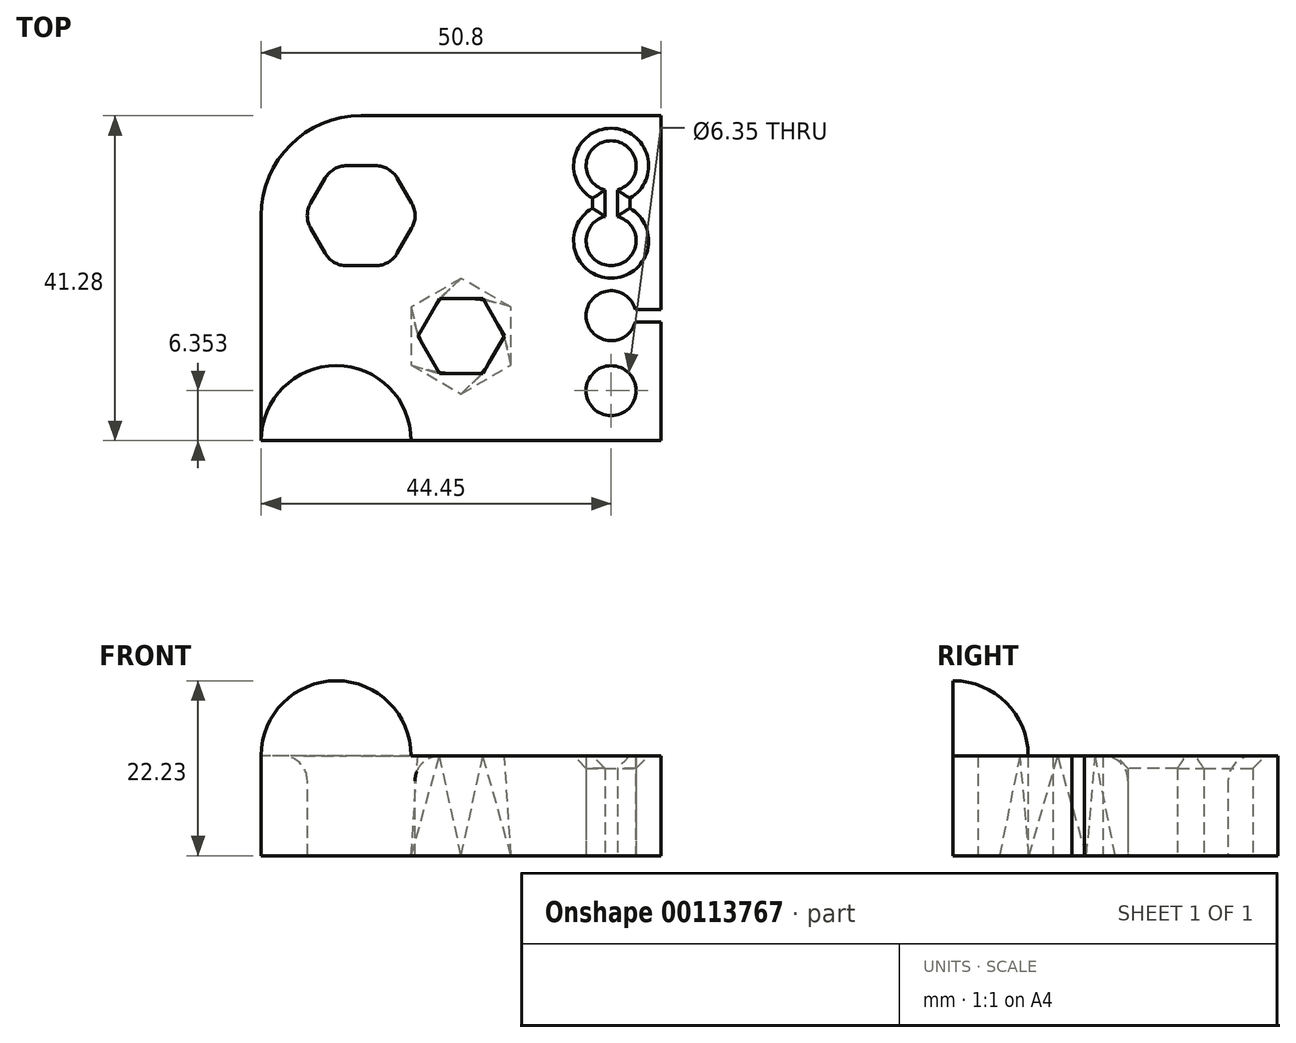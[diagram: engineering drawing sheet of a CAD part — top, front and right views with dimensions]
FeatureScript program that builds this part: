
annotation { "Feature Type Name" : "Feature", "Feature Type Description" : "" }
export const myFeature = defineFeature(function(context is Context, id is Id, definition is map)
    precondition{}
    {
        {
            var Q0;
            Q0=qCreatedBy(makeId("Top.planeOp"),FACE);
            var sketch = newSketch(context, id + "F0", { "sketchPlane" : qUnion([Q0])});
            skLineSegment(sketch, "E0.bottom", {"start": v(-12.7, 20.64) * mm, "end": v(25.4, 20.64) * mm});
            skLineSegment(sketch, "E0.top", {"start": v(-25.4, -20.64) * mm, "end": v(25.4, -20.64) * mm});
            skLineSegment(sketch, "E0.left", {"start": v(-25.4, 7.94) * mm, "end": v(-25.4, -20.64) * mm});
            skLineSegment(sketch, "E0.right", {"start": v(25.4, 20.64) * mm, "end": v(25.4, -20.64) * mm});
            skPoint(sketch, "E0.middle", {"position": v(0, 0) * mm});
            skCircle(sketch, "E1", {"center": v(19.05, -14.29) * mm, "radius": 3.18 * mm});
            skCircle(sketch, "E2.0.1.0", {"center": v(19.05, -4.76) * mm, "radius": 3.18 * mm});
            skCircle(sketch, "E2.0.2.0", {"center": v(19.05, 4.76) * mm, "radius": 3.18 * mm});
            skCircle(sketch, "E2.0.3.0", {"center": v(19.05, 14.29) * mm, "radius": 3.18 * mm});
            skLineSegment(sketch, "E2.direction1", {"start": v(19.05, -14.29) * mm, "end": v(36.43, -14.29) * mm, "construction": true});
            skLineSegment(sketch, "E2.direction2", {"start": v(19.05, -14.29) * mm, "end": v(19.05, -4.76) * mm, "construction": true});
            skLineSegment(sketch, "E3.bottom", {"start": v(18.26, -14.29) * mm, "end": v(19.84, -14.29) * mm});
            skLineSegment(sketch, "E3.top", {"start": v(18.26, 14.29) * mm, "end": v(19.84, 14.29) * mm});
            skLineSegment(sketch, "E3.left", {"start": v(18.26, -14.29) * mm, "end": v(18.26, 14.29) * mm});
            skLineSegment(sketch, "E3.right", {"start": v(19.84, -14.29) * mm, "end": v(19.84, 14.29) * mm});
            skLineSegment(sketch, "E4.bottom", {"start": v(19.05, -3.97) * mm, "end": v(25.4, -3.97) * mm});
            skLineSegment(sketch, "E4.top", {"start": v(19.05, -5.56) * mm, "end": v(25.4, -5.56) * mm});
            skLineSegment(sketch, "E4.left", {"start": v(19.05, -3.97) * mm, "end": v(19.05, -5.56) * mm});
            skLineSegment(sketch, "E4.right", {"start": v(25.4, -3.97) * mm, "end": v(25.4, -5.56) * mm});
            skPoint(sketch, "E5.visualSharp", {"position": v(-25.4, 20.64) * mm});
            skArc(sketch, "E5.filletArc", {"start": v(-12.7, 20.64) * mm, "mid": v(-21.68, 16.92) * mm, "end": v(-25.4, 7.94) * mm});
            skCircle(sketch, "E6", {"center": v(-12.7, 7.94) * mm, "radius": 6.35 * mm, "construction": true});
            skLineSegment(sketch, "E7.0", {"start": v(-9.03, 1.59) * mm, "end": v(-16.37, 1.59) * mm});
            skLineSegment(sketch, "E7.1", {"start": v(-16.37, 1.59) * mm, "end": v(-20.03, 7.94) * mm});
            skLineSegment(sketch, "E7.2", {"start": v(-20.03, 7.94) * mm, "end": v(-16.37, 14.29) * mm});
            skLineSegment(sketch, "E7.3", {"start": v(-16.37, 14.29) * mm, "end": v(-9.03, 14.29) * mm});
            skLineSegment(sketch, "E7.4", {"start": v(-9.03, 14.29) * mm, "end": v(-5.37, 7.94) * mm});
            skLineSegment(sketch, "E7.5", {"start": v(-5.37, 7.94) * mm, "end": v(-9.03, 1.59) * mm});
            skPoint(sketch, "E7.0.midPoint", {"position": v(-12.7, 1.59) * mm});
            skSolve(sketch);
        }
        {
            var Q0;
            {var subQ27=sQuery(id+"F0.wireOp",EDGE,"E0.bottom");Q0=makeQuery(id+"F0.imprint","IMPRINT",FACE,{"disambiguationData":[TD([[makeQuery(id+"F0.imprint","IMPRINT",EDGE,{"derivedFrom":subQ27}),-1.0]])]});}
            var Q1;
            {var subQ0=sQuery(id+"F0.wireOp",EDGE,"E3.left");var subQ1=sQuery(id+"F0.wireOp",EDGE,"E1");var subQ2=makeQuery(id+"F0.imprint","INTERSECT",VERTEX,{"derivedFrom":[subQ1,subQ0]});Q1=makeQuery(id+"F0.imprint","IMPRINT",FACE,{"disambiguationData":[TD([[makeQuery(id+"F0.imprint","IMPRINT",EDGE,{"disambiguationData":[TD([[subQ2,1.0]])],"derivedFrom":subQ1}),-1.0]])]});}
            var Q2;
            {var subQ0=sQuery(id+"F0.wireOp",EDGE,"E3.right");var subQ1=sQuery(id+"F0.wireOp",EDGE,"E2.0.1.0");var subQ2=makeQuery(id+"F0.imprint","INTERSECT",VERTEX,{"disambiguationData":[OD(0.0)],"derivedFrom":[subQ1,subQ0]});Q2=makeQuery(id+"F0.imprint","IMPRINT",FACE,{"disambiguationData":[TD([[makeQuery(id+"F0.imprint","IMPRINT",EDGE,{"disambiguationData":[TD([[subQ2,-1.0]])],"derivedFrom":subQ1}),-1.0]])]});}
            extrude(context, id + "F1", {"entities" : qUnion([Q0, Q1, Q2]), "depth" : 12.7 * mm});
        }
        {
            var Q0;
            Q0=makeQuery(id+"F1.opExtrude","CAP_EDGE",EDGE,{"disambiguationData":[OSD([sQuery(id+"F0.wireOp",EDGE,"E2.0.2.0")])],"isStart":false});
            var Q1;
            Q1=makeQuery(id+"F1.opExtrude","CAP_EDGE",EDGE,{"disambiguationData":[OSD([sQuery(id+"F0.wireOp",EDGE,"E2.0.3.0")])],"isStart":false});
            var Q2;
            Q2=makeQuery(id+"F1.opExtrude","CAP_EDGE",EDGE,{"disambiguationData":[OSD([sQuery(id+"F0.wireOp",EDGE,"E3.left")])],"isStart":false});
            var Q3;
            Q3=makeQuery(id+"F1.opExtrude","CAP_EDGE",EDGE,{"disambiguationData":[OSD([sQuery(id+"F0.wireOp",EDGE,"E3.right")])],"isStart":false});
            chamfer(context, id + "F2", {"entities" : qUnion([Q0, Q1, Q2, Q3]), "width" : 1.59 * mm, "tangentPropagation" : true});
        }
        {
            var Q0;
            Q0=makeQuery(id+"F1.opExtrude","CAP_EDGE",EDGE,{"disambiguationData":[OSD([sQuery(id+"F0.wireOp",EDGE,"E7.5")])],"isStart":false});
            var Q1;
            Q1=makeQuery(id+"F1.opExtrude","CAP_EDGE",EDGE,{"disambiguationData":[OSD([sQuery(id+"F0.wireOp",EDGE,"E7.4")])],"isStart":false});
            var Q2;
            Q2=makeQuery(id+"F1.opExtrude","CAP_EDGE",EDGE,{"disambiguationData":[OSD([sQuery(id+"F0.wireOp",EDGE,"E7.3")])],"isStart":false});
            var Q3;
            Q3=makeQuery(id+"F1.opExtrude","CAP_EDGE",EDGE,{"disambiguationData":[OSD([sQuery(id+"F0.wireOp",EDGE,"E7.2")])],"isStart":false});
            var Q4;
            Q4=makeQuery(id+"F1.opExtrude","CAP_EDGE",EDGE,{"disambiguationData":[OSD([sQuery(id+"F0.wireOp",EDGE,"E7.1")])],"isStart":false});
            var Q5;
            Q5=makeQuery(id+"F1.opExtrude","CAP_EDGE",EDGE,{"disambiguationData":[OSD([sQuery(id+"F0.wireOp",EDGE,"E7.0")])],"isStart":false});
            var Q6;
            Q6=makeQuery(id+"F1.opExtrude","SWEPT_EDGE",EDGE,{"disambiguationData":[OSD([sQuery(id+"F0.wireOp",EDGE,"E7.2"),sQuery(id+"F0.wireOp",EDGE,"E7.3")])]});
            var Q7;
            Q7=makeQuery(id+"F1.opExtrude","SWEPT_EDGE",EDGE,{"disambiguationData":[OSD([sQuery(id+"F0.wireOp",EDGE,"E7.1"),sQuery(id+"F0.wireOp",EDGE,"E7.2")])]});
            var Q8;
            Q8=makeQuery(id+"F1.opExtrude","SWEPT_EDGE",EDGE,{"disambiguationData":[OSD([sQuery(id+"F0.wireOp",EDGE,"E7.0"),sQuery(id+"F0.wireOp",EDGE,"E7.1")])]});
            var Q9;
            Q9=makeQuery(id+"F1.opExtrude","SWEPT_EDGE",EDGE,{"disambiguationData":[OSD([sQuery(id+"F0.wireOp",EDGE,"E7.0"),sQuery(id+"F0.wireOp",EDGE,"E7.5")])]});
            var Q10;
            Q10=makeQuery(id+"F1.opExtrude","SWEPT_EDGE",EDGE,{"disambiguationData":[OSD([sQuery(id+"F0.wireOp",EDGE,"E7.4"),sQuery(id+"F0.wireOp",EDGE,"E7.5")])]});
            var Q11;
            Q11=makeQuery(id+"F1.opExtrude","SWEPT_EDGE",EDGE,{"disambiguationData":[OSD([sQuery(id+"F0.wireOp",EDGE,"E7.3"),sQuery(id+"F0.wireOp",EDGE,"E7.4")])]});
            fillet(context, id + "F3", {"entities" : qUnion([Q0, Q1, Q2, Q3, Q4, Q5, Q6, Q7, Q8, Q9, Q10, Q11]), "radius" : 3.17 * mm, "tangentPropagation" : true, "allowEdgeOverflow" : false});
        }
        {
            var Q0;
            Q0=makeQuery(id+"F1.opExtrude","CAP_FACE",FACE,{"disambiguationData":[OSD([sQuery(id+"F0.wireOp",EDGE,"E0.bottom"),sQuery(id+"F0.wireOp",EDGE,"E0.top"),sQuery(id+"F0.wireOp",EDGE,"E0.left"),sQuery(id+"F0.wireOp",EDGE,"E0.right"),sQuery(id+"F0.wireOp",EDGE,"E1"),sQuery(id+"F0.wireOp",EDGE,"E2.0.1.0"),sQuery(id+"F0.wireOp",EDGE,"E2.0.2.0"),sQuery(id+"F0.wireOp",EDGE,"E2.0.3.0"),sQuery(id+"F0.wireOp",EDGE,"E3.left"),sQuery(id+"F0.wireOp",EDGE,"E3.right"),sQuery(id+"F0.wireOp",EDGE,"E4.bottom"),sQuery(id+"F0.wireOp",EDGE,"E4.top"),sQuery(id+"F0.wireOp",EDGE,"E5.filletArc"),sQuery(id+"F0.wireOp",EDGE,"E7.0"),sQuery(id+"F0.wireOp",EDGE,"E7.1"),sQuery(id+"F0.wireOp",EDGE,"E7.2"),sQuery(id+"F0.wireOp",EDGE,"E7.3"),sQuery(id+"F0.wireOp",EDGE,"E7.4"),sQuery(id+"F0.wireOp",EDGE,"E7.5")])],"isStart":false});
            var sketch = newSketch(context, id + "F4", { "sketchPlane" : qUnion([Q0])});
            skCircle(sketch, "E8.cCircle", {"center": v(0, -7.35) * mm, "radius": 4.76 * mm, "construction": true});
            skLineSegment(sketch, "E8.0", {"start": v(-2.75, -2.59) * mm, "end": v(2.75, -2.59) * mm});
            skLineSegment(sketch, "E8.1", {"start": v(2.75, -2.59) * mm, "end": v(5.5, -7.35) * mm});
            skLineSegment(sketch, "E8.2", {"start": v(5.5, -7.35) * mm, "end": v(2.75, -12.11) * mm});
            skLineSegment(sketch, "E8.3", {"start": v(2.75, -12.11) * mm, "end": v(-2.75, -12.11) * mm});
            skLineSegment(sketch, "E8.4", {"start": v(-2.75, -12.11) * mm, "end": v(-5.5, -7.35) * mm});
            skLineSegment(sketch, "E8.5", {"start": v(-5.5, -7.35) * mm, "end": v(-2.75, -2.59) * mm});
            skPoint(sketch, "E8.0.midPoint", {"position": v(0, -2.59) * mm});
            skSolve(sketch);
        }
        {
            var Q0;
            Q0=makeQuery(id+"F1.opExtrude","CAP_FACE",FACE,{"disambiguationData":[OSD([sQuery(id+"F0.wireOp",EDGE,"E0.bottom"),sQuery(id+"F0.wireOp",EDGE,"E0.top"),sQuery(id+"F0.wireOp",EDGE,"E0.left"),sQuery(id+"F0.wireOp",EDGE,"E0.right"),sQuery(id+"F0.wireOp",EDGE,"E1"),sQuery(id+"F0.wireOp",EDGE,"E2.0.1.0"),sQuery(id+"F0.wireOp",EDGE,"E2.0.2.0"),sQuery(id+"F0.wireOp",EDGE,"E2.0.3.0"),sQuery(id+"F0.wireOp",EDGE,"E3.left"),sQuery(id+"F0.wireOp",EDGE,"E3.right"),sQuery(id+"F0.wireOp",EDGE,"E4.bottom"),sQuery(id+"F0.wireOp",EDGE,"E4.top"),sQuery(id+"F0.wireOp",EDGE,"E5.filletArc"),sQuery(id+"F0.wireOp",EDGE,"E7.0"),sQuery(id+"F0.wireOp",EDGE,"E7.1"),sQuery(id+"F0.wireOp",EDGE,"E7.2"),sQuery(id+"F0.wireOp",EDGE,"E7.3"),sQuery(id+"F0.wireOp",EDGE,"E7.4"),sQuery(id+"F0.wireOp",EDGE,"E7.5")])],"isStart":true});
            var sketch = newSketch(context, id + "F5", { "sketchPlane" : qUnion([Q0])});
            skPoint(sketch, "E9.0", {"position": v(0, 7.35) * mm});
            skCircle(sketch, "E10.cCircle", {"center": v(0, 7.35) * mm, "radius": 6.35 * mm, "construction": true});
            skLineSegment(sketch, "E10.0", {"start": v(-6.35, 3.69) * mm, "end": v(-6.35, 11.02) * mm});
            skLineSegment(sketch, "E10.1", {"start": v(-6.35, 11.02) * mm, "end": v(0, 14.68) * mm});
            skLineSegment(sketch, "E10.2", {"start": v(0, 14.68) * mm, "end": v(6.35, 11.02) * mm});
            skLineSegment(sketch, "E10.3", {"start": v(6.35, 11.02) * mm, "end": v(6.35, 3.69) * mm});
            skLineSegment(sketch, "E10.4", {"start": v(6.35, 3.69) * mm, "end": v(0, 0.02) * mm});
            skLineSegment(sketch, "E10.5", {"start": v(0, 0.02) * mm, "end": v(-6.35, 3.69) * mm});
            skPoint(sketch, "E10.0.midPoint", {"position": v(-6.35, 7.35) * mm});
            skSolve(sketch);
        }
        {
            var Q1;
            Q1=makeQuery(id+"F5.imprint","IMPRINT",FACE,{"disambiguationData":[TD([[makeQuery(id+"F5.imprint","IMPRINT",EDGE,{"derivedFrom":sQuery(id+"F5.wireOp",EDGE,"E10.0")}),-1.0]])]});
            var Q2;
            Q2=makeQuery(id+"F4.imprint","IMPRINT",FACE,{"disambiguationData":[TD([[makeQuery(id+"F4.imprint","IMPRINT",EDGE,{"derivedFrom":sQuery(id+"F4.wireOp",EDGE,"E8.0")}),-1.0]])]});
            loft(context, id + "F6", {"operationType" : NewBodyOperationType.REMOVE, "sheetProfilesArray" : [{ "sheetProfileEntities" : qUnion([Q1]) }, { "sheetProfileEntities" : qUnion([Q2]) }]});
        }
        {
            var Q0;
            Q0=makeQuery(id+"F1.opExtrude","SWEPT_FACE",FACE,{"disambiguationData":[OSD([sQuery(id+"F0.wireOp",EDGE,"E0.top")])]});
            var sketch = newSketch(context, id + "F7", { "sketchPlane" : qUnion([Q0])});
            skCircle(sketch, "E11", {"center": v(-15.88, 12.7) * mm, "radius": 9.53 * mm});
            skLineSegment(sketch, "E12", {"start": v(-25.4, 12.7) * mm, "end": v(-6.35, 12.7) * mm});
            skSolve(sketch);
        }
        {
            var Q0;
            {var subQ0=sQuery(id+"F7.wireOp",EDGE,"E12");Q0=makeQuery(id+"F7.imprint","IMPRINT",FACE,{"disambiguationData":[TD([[makeQuery(id+"F7.imprint","IMPRINT",EDGE,{"derivedFrom":subQ0}),1.0]])]});}
            var Q1;
            Q1=sQuery(id+"F7.wireOp",EDGE,"E12");
            revolve(context, id + "F8", {"operationType" : NewBodyOperationType.ADD, "entities" : qUnion([Q0]), "axis" : qUnion([Q1]), "revolveType" : RevolveType.ONE_DIRECTION, "oppositeDirection" : true, "angle" : 90 * degree});
        }
    });
